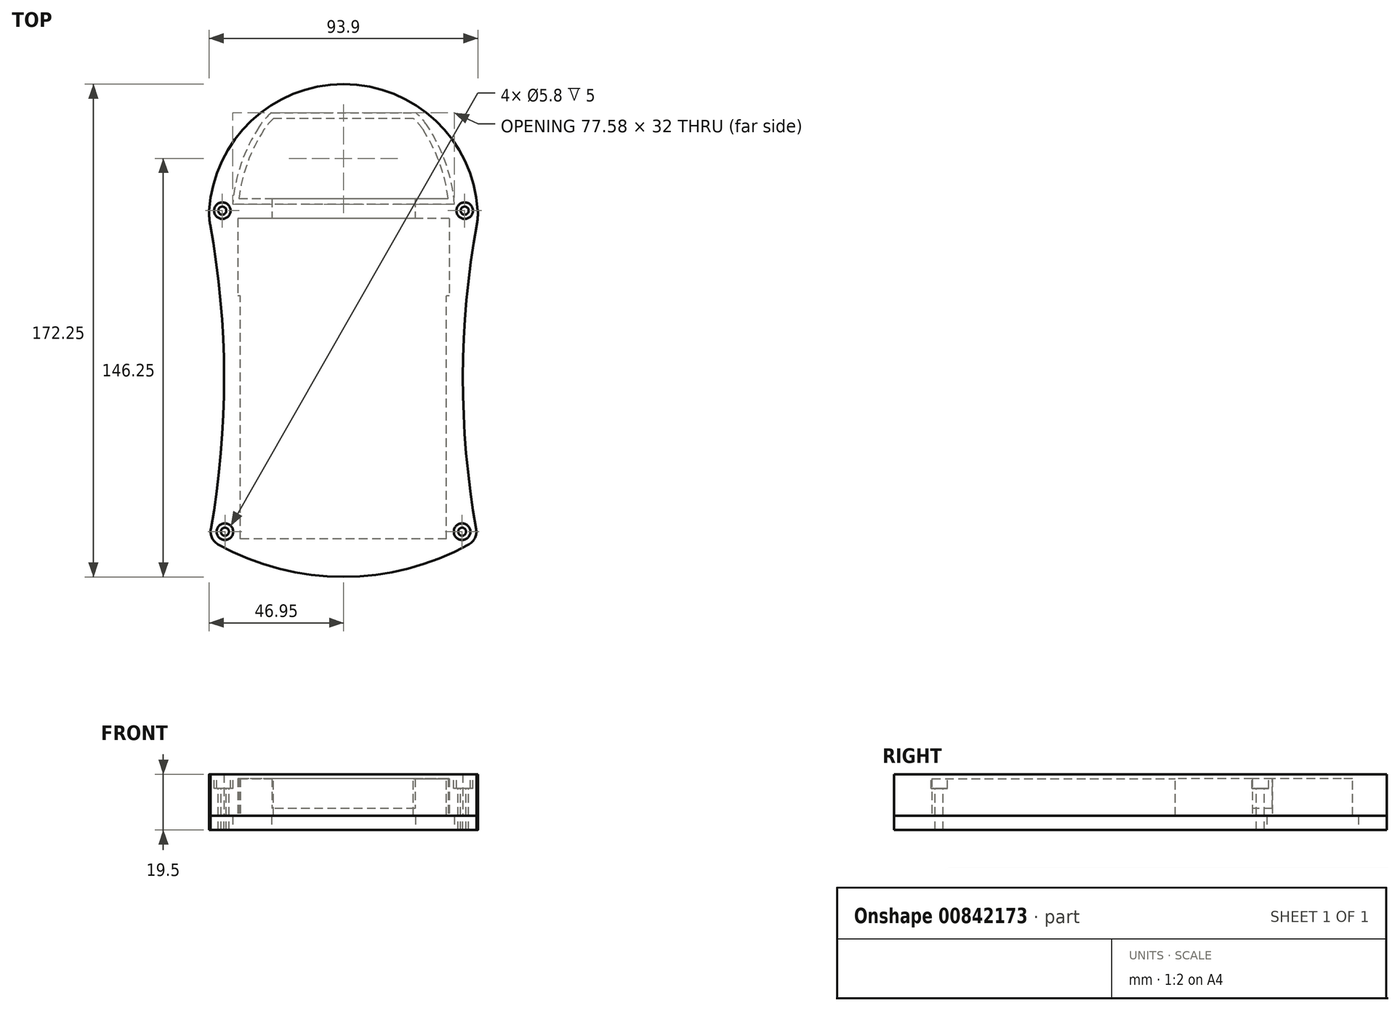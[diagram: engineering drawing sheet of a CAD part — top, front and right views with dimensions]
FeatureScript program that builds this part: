
annotation { "Feature Type Name" : "Feature", "Feature Type Description" : "" }
export const myFeature = defineFeature(function(context is Context, id is Id, definition is map)
    precondition{}
    {
        {
            var Q0;
            Q0=qCreatedBy(makeId("Top.planeOp"),FACE);
            var sketch = newSketch(context, id + "F0", { "sketchPlane" : qUnion([Q0])});
            skLineSegment(sketch, "E0.bottom", {"start": v(36, -56) * mm, "end": v(-36, -56) * mm});
            skLineSegment(sketch, "E0.top", {"start": v(36, 56) * mm, "end": v(-36, 56) * mm});
            skLineSegment(sketch, "E0.left", {"start": v(36, -56) * mm, "end": v(36, 56) * mm});
            skLineSegment(sketch, "E0.right", {"start": v(-36, -56) * mm, "end": v(-36, 56) * mm});
            skPoint(sketch, "E0.middle", {"position": v(0, 0) * mm});
            skArc(sketch, "E1", {"start": v(47, 56) * mm, "mid": v(0, 103) * mm, "end": v(-47, 56) * mm});
            skArc(sketch, "E2", {"start": v(-47, -56) * mm, "mid": v(-41.73, 0) * mm, "end": v(-47, 56) * mm});
            skLineSegment(sketch, "E3", {"start": v(0, 117.63) * mm, "end": v(0, -101.58) * mm, "construction": true});
            skLineSegment(sketch, "E4", {"start": v(-114.42, 0) * mm, "end": v(113.04, 0) * mm, "construction": true});
            skArc(sketch, "E5.MirrorCS", {"start": v(47, -56) * mm, "mid": v(0, -103) * mm, "end": v(-47, -56) * mm});
            skArc(sketch, "E6.MirrorCS", {"start": v(47, -56) * mm, "mid": v(41.73, 0) * mm, "end": v(47, 56) * mm});
            skSolve(sketch);
        }
        {
            var Q0;
            Q0=makeQuery(id+"F0.imprint","IMPRINT",FACE,{"disambiguationData":[TD([[makeQuery(id+"F0.imprint","IMPRINT",EDGE,{"derivedFrom":sQuery(id+"F0.wireOp",EDGE,"E0.bottom")}),1.0]])]});
            extrude(context, id + "F1", {"entities" : qUnion([Q0]), "depth" : 14.5 * mm, "offsetDistance" : 25 * mm});
        }
        {
            var Q0;
            Q0=makeQuery(id+"F1.opExtrude","CAP_FACE",FACE,{"disambiguationData":[OSD([sQuery(id+"F0.wireOp",EDGE,"E0.bottom"),sQuery(id+"F0.wireOp",EDGE,"E0.top"),sQuery(id+"F0.wireOp",EDGE,"E0.left"),sQuery(id+"F0.wireOp",EDGE,"E0.right"),sQuery(id+"F0.wireOp",EDGE,"E1"),sQuery(id+"F0.wireOp",EDGE,"E2"),sQuery(id+"F0.wireOp",EDGE,"E5.MirrorCS"),sQuery(id+"F0.wireOp",EDGE,"E6.MirrorCS")])],"isStart":false});
            var sketch = newSketch(context, id + "F2", { "sketchPlane" : qUnion([Q0])});
            skLineSegment(sketch, "E7.bottom", {"start": v(36, -56) * mm, "end": v(-36, -56) * mm});
            skLineSegment(sketch, "E7.top", {"start": v(36, 56) * mm, "end": v(-36, 56) * mm});
            skLineSegment(sketch, "E7.left", {"start": v(36, -56) * mm, "end": v(36, 56) * mm});
            skLineSegment(sketch, "E7.right", {"start": v(-36, -56) * mm, "end": v(-36, 56) * mm});
            skPoint(sketch, "E7.middle", {"position": v(0, 0) * mm});
            skSolve(sketch);
        }
        {
            var Q0;
            Q0 = qSketchRegion(id + "F2", true);
            extrude(context, id + "F3", {"entities" : qUnion([Q0]), "operationType" : NewBodyOperationType.ADD, "oppositeDirection" : true, "depth" : 1.5 * mm, "offsetDistance" : 25 * mm});
        }
        {
            var Q0;
            Q0=makeQuery(id+"F1.opExtrude","CAP_FACE",FACE,{"disambiguationData":[OSD([sQuery(id+"F0.wireOp",EDGE,"E0.bottom"),sQuery(id+"F0.wireOp",EDGE,"E0.top"),sQuery(id+"F0.wireOp",EDGE,"E0.left"),sQuery(id+"F0.wireOp",EDGE,"E0.right"),sQuery(id+"F0.wireOp",EDGE,"E1"),sQuery(id+"F0.wireOp",EDGE,"E2"),sQuery(id+"F0.wireOp",EDGE,"E5.MirrorCS"),sQuery(id+"F0.wireOp",EDGE,"E6.MirrorCS")])],"isStart":true});
            var sketch = newSketch(context, id + "F4", { "sketchPlane" : qUnion([Q0])});
            skLineSegment(sketch, "E8", {"start": v(0, -56) * mm, "end": v(0, -29) * mm, "construction": true});
            skLineSegment(sketch, "E9.bottom", {"start": v(37, -56) * mm, "end": v(-37, -56) * mm});
            skLineSegment(sketch, "E9.top", {"start": v(37, -29) * mm, "end": v(-37, -29) * mm});
            skLineSegment(sketch, "E9.left", {"start": v(37, -56) * mm, "end": v(37, -29) * mm});
            skLineSegment(sketch, "E9.right", {"start": v(-37, -56) * mm, "end": v(-37, -29) * mm});
            skPoint(sketch, "E9.middle", {"position": v(0, -42.5) * mm});
            skSolve(sketch);
        }
        {
            var Q0;
            Q0 = qSketchRegion(id + "F4", true);
            var Q1;
            Q1=makeQuery(id+"F3.opExtrude","CAP_FACE",FACE,{"disambiguationData":[OSD([sQuery(id+"F2.wireOp",EDGE,"E7.bottom"),sQuery(id+"F2.wireOp",EDGE,"E7.top"),sQuery(id+"F2.wireOp",EDGE,"E7.left"),sQuery(id+"F2.wireOp",EDGE,"E7.right")])],"isStart":false});
            extrude(context, id + "F5", {"entities" : qUnion([Q0]), "operationType" : NewBodyOperationType.REMOVE, "endBound" : BoundingType.UP_TO_SURFACE, "oppositeDirection" : true, "depth" : 25 * mm, "endBoundEntityFace" : qUnion([Q1]), "offsetDistance" : 25 * mm});
        }
        {
            var Q0;
            Q0=makeQuery(id+"F1.opExtrude","CAP_FACE",FACE,{"disambiguationData":[OSD([sQuery(id+"F0.wireOp",EDGE,"E0.bottom"),sQuery(id+"F0.wireOp",EDGE,"E0.top"),sQuery(id+"F0.wireOp",EDGE,"E0.left"),sQuery(id+"F0.wireOp",EDGE,"E0.right"),sQuery(id+"F0.wireOp",EDGE,"E1"),sQuery(id+"F0.wireOp",EDGE,"E2"),sQuery(id+"F0.wireOp",EDGE,"E5.MirrorCS"),sQuery(id+"F0.wireOp",EDGE,"E6.MirrorCS")])],"isStart":true});
            var sketch = newSketch(context, id + "F6", { "sketchPlane" : qUnion([Q0])});
            skArc(sketch, "E10", {"start": v(47, 56) * mm, "mid": v(0, 69.25) * mm, "end": v(-47, 56) * mm});
            skArc(sketch, "E11.0", {"start": v(47, 56) * mm, "mid": v(0, 103) * mm, "end": v(-47, 56) * mm});
            skSolve(sketch);
        }
        {
            var Q0;
            Q0 = qSketchRegion(id + "F6", true);
            extrude(context, id + "F7", {"entities" : qUnion([Q0]), "operationType" : NewBodyOperationType.REMOVE, "oppositeDirection" : true, "depth" : 25 * mm, "offsetDistance" : 25 * mm});
        }
        {
            var Q0;
            Q0=makeQuery(id+"F1.opExtrude","CAP_FACE",FACE,{"disambiguationData":[OSD([sQuery(id+"F0.wireOp",EDGE,"E0.bottom"),sQuery(id+"F0.wireOp",EDGE,"E0.top"),sQuery(id+"F0.wireOp",EDGE,"E0.left"),sQuery(id+"F0.wireOp",EDGE,"E0.right"),sQuery(id+"F0.wireOp",EDGE,"E1"),sQuery(id+"F0.wireOp",EDGE,"E2"),sQuery(id+"F0.wireOp",EDGE,"E5.MirrorCS"),sQuery(id+"F0.wireOp",EDGE,"E6.MirrorCS")])],"isStart":true});
            var sketch = newSketch(context, id + "F8", { "sketchPlane" : qUnion([Q0])});
            skArc(sketch, "E12", {"start": v(27.76, -87.12) * mm, "mid": v(33.54, -75.56) * mm, "end": v(36.57, -63) * mm});
            skLineSegment(sketch, "E13", {"start": v(0, 109.51) * mm, "end": v(0, -146.95) * mm, "construction": true});
            skArc(sketch, "E14.MirrorCS", {"start": v(-27.76, -87.12) * mm, "mid": v(-33.54, -75.56) * mm, "end": v(-36.57, -63) * mm});
            skLineSegment(sketch, "E15", {"start": v(-36.57, -63) * mm, "end": v(36.57, -63) * mm});
            skPoint(sketch, "E16.orphan", {"position": v(-47, -56) * mm});
            skPoint(sketch, "E17.orphan", {"position": v(47, -56) * mm});
            skPoint(sketch, "E18.orphan", {"position": v(37, -56) * mm});
            skPoint(sketch, "E19.orphan", {"position": v(-37, -56) * mm});
            skArc(sketch, "E20.0", {"start": v(20.57, -93.76) * mm, "mid": v(0, -99) * mm, "end": v(-20.57, -93.76) * mm});
            skPoint(sketch, "E21.orphan", {"position": v(-16, -100.2) * mm});
            skPoint(sketch, "E22.orphan", {"position": v(16, -100.2) * mm});
            skPoint(sketch, "E23.visualSharp", {"position": v(-25, -90.99) * mm});
            skArc(sketch, "E23.filletArc", {"start": v(-27.76, -87.12) * mm, "mid": v(-24.57, -90.89) * mm, "end": v(-20.57, -93.76) * mm});
            skPoint(sketch, "E24.visualSharp", {"position": v(25, -90.99) * mm});
            skArc(sketch, "E24.filletArc", {"start": v(20.57, -93.76) * mm, "mid": v(24.57, -90.89) * mm, "end": v(27.76, -87.12) * mm});
            skSolve(sketch);
        }
        {
            var Q0;
            Q0 = qSketchRegion(id + "F8", true);
            extrude(context, id + "F9", {"entities" : qUnion([Q0]), "operationType" : NewBodyOperationType.REMOVE, "oppositeDirection" : true, "depth" : 13 * mm, "offsetDistance" : 25 * mm});
        }
        {
            var Q0;
            Q0=makeQuery(id+"F1.opExtrude","SWEPT_EDGE",EDGE,{"disambiguationData":[OSD([sQuery(id+"F0.wireOp",EDGE,"E1"),sQuery(id+"F0.wireOp",EDGE,"E2")])]});
            var Q1;
            Q1=makeQuery(id+"F1.opExtrude","SWEPT_EDGE",EDGE,{"disambiguationData":[OSD([sQuery(id+"F0.wireOp",EDGE,"E1"),sQuery(id+"F0.wireOp",EDGE,"E6.MirrorCS")])]});
            fillet(context, id + "F10", {"entities" : qUnion([Q0, Q1]), "radius" : 20 * mm, "tangentPropagation" : true, "allowEdgeOverflow" : false});
        }
        {
            var Q0;
            {var subQ0=sQuery(id+"F0.wireOp",EDGE,"E6.MirrorCS");Q0=makeQuery(id+"F7.boolean.opBoolean","MERGE",EDGE,{"derivedFrom":[makeQuery(id+"F1.opExtrude","SWEPT_EDGE",EDGE,{"disambiguationData":[OSD([sQuery(id+"F0.wireOp",EDGE,"E5.MirrorCS"),subQ0])]}),makeQuery(id+"F7.opExtrude","SWEPT_EDGE",EDGE,{"disambiguationData":[OSD([subQ0,sQuery(id+"F6.wireOp",EDGE,"E10"),sQuery(id+"F6.wireOp",EDGE,"E11.0")])]})]});}
            var Q1;
            {var subQ0=sQuery(id+"F0.wireOp",EDGE,"E2");Q1=makeQuery(id+"F7.boolean.opBoolean","MERGE",EDGE,{"derivedFrom":[makeQuery(id+"F1.opExtrude","SWEPT_EDGE",EDGE,{"disambiguationData":[OSD([subQ0,sQuery(id+"F0.wireOp",EDGE,"E5.MirrorCS")])]}),makeQuery(id+"F7.opExtrude","SWEPT_EDGE",EDGE,{"disambiguationData":[OSD([subQ0,sQuery(id+"F6.wireOp",EDGE,"E10"),sQuery(id+"F6.wireOp",EDGE,"E11.0")])]})]});}
            fillet(context, id + "F11", {"entities" : qUnion([Q0, Q1]), "radius" : 5 * mm, "tangentPropagation" : true, "allowEdgeOverflow" : false});
        }
        {
            var Q0;
            Q0=makeQuery(id+"F3.boolean.opBoolean","MERGE",FACE,{"derivedFrom":[makeQuery(id+"F1.opExtrude","CAP_FACE",FACE,{"disambiguationData":[OSD([sQuery(id+"F0.wireOp",EDGE,"E0.bottom"),sQuery(id+"F0.wireOp",EDGE,"E0.top"),sQuery(id+"F0.wireOp",EDGE,"E0.left"),sQuery(id+"F0.wireOp",EDGE,"E0.right"),sQuery(id+"F0.wireOp",EDGE,"E1"),sQuery(id+"F0.wireOp",EDGE,"E2"),sQuery(id+"F0.wireOp",EDGE,"E5.MirrorCS"),sQuery(id+"F0.wireOp",EDGE,"E6.MirrorCS")])],"isStart":false}),makeQuery(id+"F3.opExtrude","CAP_FACE",FACE,{"disambiguationData":[OSD([sQuery(id+"F2.wireOp",EDGE,"E7.bottom"),sQuery(id+"F2.wireOp",EDGE,"E7.top"),sQuery(id+"F2.wireOp",EDGE,"E7.left"),sQuery(id+"F2.wireOp",EDGE,"E7.right")])],"isStart":true})]});
            var sketch = newSketch(context, id + "F12", { "sketchPlane" : qUnion([Q0])});
            skCircle(sketch, "E25", {"center": v(-42.35, 58.78) * mm, "radius": 2.9 * mm});
            skLineSegment(sketch, "E26", {"start": v(0, 101.03) * mm, "end": v(0, -86.28) * mm, "construction": true});
            skCircle(sketch, "E27.MirrorC", {"center": v(42.35, 58.78) * mm, "radius": 2.9 * mm});
            skCircle(sketch, "E28", {"center": v(-41.45, -53.46) * mm, "radius": 2.9 * mm});
            skCircle(sketch, "E29.MirrorC", {"center": v(41.45, -53.46) * mm, "radius": 2.9 * mm});
            skSolve(sketch);
        }
        {
            var Q0;
            Q0 = qSketchRegion(id + "F12", true);
            extrude(context, id + "F13", {"entities" : qUnion([Q0]), "operationType" : NewBodyOperationType.REMOVE, "oppositeDirection" : true, "depth" : 5 * mm, "offsetDistance" : 25 * mm});
        }
        {
            var Q0;
            Q0=makeQuery(id+"F13.boolean.opBoolean","COPY",FACE,{"derivedFrom":makeQuery(id+"F13.opExtrude","CAP_FACE",FACE,{"disambiguationData":[OSD([sQuery(id+"F12.wireOp",EDGE,"E25")])],"isStart":false})});
            var sketch = newSketch(context, id + "F14", { "sketchPlane" : qUnion([Q0])});
            skCircle(sketch, "E30", {"center": v(-42.35, 58.78) * mm, "radius": 1.4 * mm});
            skLineSegment(sketch, "E31", {"start": v(0, 85.8) * mm, "end": v(0, -75.06) * mm, "construction": true});
            skCircle(sketch, "E32", {"center": v(-41.45, -53.46) * mm, "radius": 1.4 * mm});
            skCircle(sketch, "E33.MirrorC", {"center": v(42.35, 58.78) * mm, "radius": 1.4 * mm});
            skCircle(sketch, "E34.MirrorC", {"center": v(41.45, -53.46) * mm, "radius": 1.4 * mm});
            skSolve(sketch);
        }
        {
            var Q0;
            Q0 = qSketchRegion(id + "F14", true);
            extrude(context, id + "F15", {"entities" : qUnion([Q0]), "operationType" : NewBodyOperationType.REMOVE, "oppositeDirection" : true, "depth" : 25 * mm, "offsetDistance" : 25 * mm});
        }
        {
            var Q0;
            Q0=makeQuery(id+"F5.boolean.opBoolean","MERGE",FACE,{"derivedFrom":[makeQuery(id+"F1.opExtrude","SWEPT_FACE",FACE,{"disambiguationData":[OSD([sQuery(id+"F0.wireOp",EDGE,"E0.top")])]}),makeQuery(id+"F5.opExtrude","SWEPT_FACE",FACE,{"disambiguationData":[OSD([sQuery(id+"F4.wireOp",EDGE,"E9.bottom")])]})]});
            var sketch = newSketch(context, id + "F16", { "sketchPlane" : qUnion([Q0])});
            skLineSegment(sketch, "E35.bottom", {"start": v(-25, 13) * mm, "end": v(25, 13) * mm});
            skLineSegment(sketch, "E35.left", {"start": v(-25, 13) * mm, "end": v(-25, 2.5) * mm});
            skLineSegment(sketch, "E35.right", {"start": v(25, 13) * mm, "end": v(25, 2.5) * mm});
            skPoint(sketch, "E35.middle", {"position": v(0, 6.5) * mm});
            skLineSegment(sketch, "E36", {"start": v(25, 2.5) * mm, "end": v(-25, 2.5) * mm});
            skPoint(sketch, "E37.orphan", {"position": v(25, 0) * mm});
            skPoint(sketch, "E38.orphan", {"position": v(-25, 0) * mm});
            skSolve(sketch);
        }
        {
            var Q0;
            Q0 = qSketchRegion(id + "F16", true);
            extrude(context, id + "F17", {"entities" : qUnion([Q0]), "operationType" : NewBodyOperationType.REMOVE, "oppositeDirection" : true, "depth" : 25 * mm, "offsetDistance" : 25 * mm});
        }
        {
            var Q0;
            Q0=makeQuery(id+"F9.boolean.opBoolean","COPY",FACE,{"derivedFrom":makeQuery(id+"F9.opExtrude","CAP_FACE",FACE,{"disambiguationData":[OSD([sQuery(id+"F8.wireOp",EDGE,"E12"),sQuery(id+"F8.wireOp",EDGE,"E14.MirrorCS"),sQuery(id+"F8.wireOp",EDGE,"E15"),sQuery(id+"F8.wireOp",EDGE,"E20.0"),sQuery(id+"F8.wireOp",EDGE,"E23.filletArc"),sQuery(id+"F8.wireOp",EDGE,"E24.filletArc")])],"isStart":false})});
            var sketch = newSketch(context, id + "F18", { "sketchPlane" : qUnion([Q0])});
            skPoint(sketch, "E39", {"position": v(24.45, -91) * mm});
            skLineSegment(sketch, "E40", {"start": v(24.45, -91) * mm, "end": v(-24.45, -91) * mm});
            skArc(sketch, "E41.0", {"start": v(-24.45, -91) * mm, "mid": v(-22.6, -92.5) * mm, "end": v(-20.57, -93.76) * mm});
            skArc(sketch, "E42.0", {"start": v(20.57, -93.76) * mm, "mid": v(0, -99) * mm, "end": v(-20.57, -93.76) * mm});
            skArc(sketch, "E43.0", {"start": v(20.57, -93.76) * mm, "mid": v(22.6, -92.5) * mm, "end": v(24.45, -91) * mm});
            skPoint(sketch, "E44.orphan", {"position": v(-27.76, -87.12) * mm});
            skPoint(sketch, "E45.orphan", {"position": v(27.76, -87.12) * mm});
            skSolve(sketch);
        }
        {
            var Q0;
            Q0 = qSketchRegion(id + "F18", true);
            var Q1;
            Q1=makeQuery(id+"F1.opExtrude","CAP_FACE",FACE,{"disambiguationData":[OSD([sQuery(id+"F0.wireOp",EDGE,"E0.bottom"),sQuery(id+"F0.wireOp",EDGE,"E0.top"),sQuery(id+"F0.wireOp",EDGE,"E0.left"),sQuery(id+"F0.wireOp",EDGE,"E0.right"),sQuery(id+"F0.wireOp",EDGE,"E1"),sQuery(id+"F0.wireOp",EDGE,"E2"),sQuery(id+"F0.wireOp",EDGE,"E5.MirrorCS"),sQuery(id+"F0.wireOp",EDGE,"E6.MirrorCS")])],"isStart":true});
            extrude(context, id + "F19", {"entities" : qUnion([Q0]), "operationType" : NewBodyOperationType.ADD, "endBound" : BoundingType.UP_TO_SURFACE, "depth" : 25 * mm, "endBoundEntityFace" : qUnion([Q1]), "offsetDistance" : 25 * mm});
        }
        {
            var Q0;
            {var subQ0=sQuery(id+"F0.wireOp",EDGE,"E6.MirrorCS");var subQ1=sQuery(id+"F0.wireOp",EDGE,"E5.MirrorCS");var subQ2=sQuery(id+"F0.wireOp",EDGE,"E2");var subQ3=sQuery(id+"F0.wireOp",EDGE,"E1");var subQ4=sQuery(id+"F0.wireOp",EDGE,"E0.right");var subQ5=sQuery(id+"F0.wireOp",EDGE,"E0.left");var subQ6=sQuery(id+"F0.wireOp",EDGE,"E0.top");var subQ7=sQuery(id+"F0.wireOp",EDGE,"E0.bottom");Q0=makeQuery(id+"F19.boolean.opBoolean","MERGE",FACE,{"derivedFrom":[makeQuery(id+"F1.opExtrude","CAP_FACE",FACE,{"disambiguationData":[OSD([subQ7,subQ6,subQ5,subQ4,subQ3,subQ2,subQ1,subQ0])],"isStart":true}),makeQuery(id+"F19.opExtrude","CAP_FACE",FACE,{"disambiguationData":[OSD([subQ7,subQ6,subQ5,subQ4,subQ3,subQ2,subQ1,subQ0])],"isStart":false})]});}
            var sketch = newSketch(context, id + "F20", { "sketchPlane" : qUnion([Q0])});
            skArc(sketch, "E46.0.0", {"start": v(46.63, -54) * mm, "mid": v(41.73, -0.72) * mm, "end": v(46.37, 52.58) * mm});
            skArc(sketch, "E46.0.1", {"start": v(46.37, 52.58) * mm, "mid": v(45.97, 55.6) * mm, "end": v(43.89, 57.82) * mm});
            skArc(sketch, "E46.0.2", {"start": v(43.89, 57.82) * mm, "mid": v(0, 69.25) * mm, "end": v(-43.89, 57.82) * mm});
            skArc(sketch, "E46.0.3", {"start": v(-43.89, 57.82) * mm, "mid": v(-45.97, 55.6) * mm, "end": v(-46.37, 52.58) * mm});
            skArc(sketch, "E46.0.4", {"start": v(-46.37, 52.58) * mm, "mid": v(-41.73, -0.72) * mm, "end": v(-46.63, -54) * mm});
            skArc(sketch, "E46.0.5", {"start": v(-46.63, -54) * mm, "mid": v(-46.92, -56.38) * mm, "end": v(-46.92, -58.78) * mm});
            skArc(sketch, "E46.0.6", {"start": v(-46.92, -58.78) * mm, "mid": v(0, -103) * mm, "end": v(46.92, -58.78) * mm});
            skArc(sketch, "E46.0.7", {"start": v(46.92, -58.78) * mm, "mid": v(46.92, -56.38) * mm, "end": v(46.63, -54) * mm});
            skCircle(sketch, "E47.0", {"center": v(-42.35, -58.78) * mm, "radius": 1.4 * mm});
            skCircle(sketch, "E48.0", {"center": v(42.35, -58.78) * mm, "radius": 1.4 * mm});
            skCircle(sketch, "E49.0", {"center": v(-41.45, 53.46) * mm, "radius": 1.4 * mm});
            skCircle(sketch, "E50.0", {"center": v(41.45, 53.46) * mm, "radius": 1.4 * mm});
            skSolve(sketch);
        }
        {
            var Q0;
            Q0 = qSketchRegion(id + "F20", true);
            extrude(context, id + "F21", {"entities" : qUnion([Q0]), "depth" : 5 * mm, "offsetDistance" : 25 * mm});
        }
        {
            var Q0;
            Q0=makeQuery(id+"F21.opExtrude","CAP_FACE",FACE,{"disambiguationData":[OSD([sQuery(id+"F20.wireOp",EDGE,"E46.0.0"),sQuery(id+"F20.wireOp",EDGE,"E46.0.1"),sQuery(id+"F20.wireOp",EDGE,"E46.0.2"),sQuery(id+"F20.wireOp",EDGE,"E46.0.3"),sQuery(id+"F20.wireOp",EDGE,"E46.0.4"),sQuery(id+"F20.wireOp",EDGE,"E46.0.5"),sQuery(id+"F20.wireOp",EDGE,"E46.0.6"),sQuery(id+"F20.wireOp",EDGE,"E46.0.7"),sQuery(id+"F20.wireOp",EDGE,"E47.0"),sQuery(id+"F20.wireOp",EDGE,"E48.0"),sQuery(id+"F20.wireOp",EDGE,"E49.0"),sQuery(id+"F20.wireOp",EDGE,"E50.0")])],"isStart":false});
            var sketch = newSketch(context, id + "F22", { "sketchPlane" : qUnion([Q0])});
            skLineSegment(sketch, "E51.0.0", {"start": v(-24.45, -91) * mm, "end": v(24.45, -91) * mm});
            skArc(sketch, "E51.0.1", {"start": v(24.45, -91) * mm, "mid": v(26.23, -89.16) * mm, "end": v(27.76, -87.12) * mm});
            skArc(sketch, "E51.0.2", {"start": v(27.76, -87.12) * mm, "mid": v(33.54, -75.56) * mm, "end": v(36.57, -63) * mm});
            skLineSegment(sketch, "E51.0.3", {"start": v(36.57, -63) * mm, "end": v(-36.57, -63) * mm});
            skArc(sketch, "E51.0.4", {"start": v(-36.57, -63) * mm, "mid": v(-33.54, -75.56) * mm, "end": v(-27.76, -87.12) * mm});
            skArc(sketch, "E51.0.5", {"start": v(-27.76, -87.12) * mm, "mid": v(-26.23, -89.16) * mm, "end": v(-24.45, -91) * mm});
            skArc(sketch, "E52.0", {"start": v(29.43, -88.2) * mm, "mid": v(35.8, -75.18) * mm, "end": v(38.79, -61) * mm});
            skArc(sketch, "E52.1", {"start": v(-38.79, -61) * mm, "mid": v(-35.8, -75.18) * mm, "end": v(-29.43, -88.2) * mm});
            skArc(sketch, "E52.2", {"start": v(-29.43, -88.2) * mm, "mid": v(-27.5, -90.76) * mm, "end": v(-25.2, -93) * mm});
            skLineSegment(sketch, "E52.3", {"start": v(38.79, -61) * mm, "end": v(-38.79, -61) * mm});
            skLineSegment(sketch, "E52.4", {"start": v(-25.2, -93) * mm, "end": v(25.2, -93) * mm});
            skArc(sketch, "E52.5", {"start": v(25.2, -93) * mm, "mid": v(27.5, -90.76) * mm, "end": v(29.43, -88.2) * mm});
            skSolve(sketch);
        }
        {
            var Q0;
            Q0=makeQuery(id+"F22.imprint","IMPRINT",FACE,{"disambiguationData":[TD([[makeQuery(id+"F22.imprint","IMPRINT",EDGE,{"derivedFrom":sQuery(id+"F22.wireOp",EDGE,"E51.0.0")}),-1.0]])]});
            var Q1;
            Q1=makeQuery(id+"F22.imprint","IMPRINT",FACE,{"disambiguationData":[TD([[makeQuery(id+"F22.imprint","IMPRINT",EDGE,{"derivedFrom":sQuery(id+"F22.wireOp",EDGE,"E51.0.0")}),1.0]])]});
            extrude(context, id + "F23", {"entities" : qUnion([Q0, Q1]), "operationType" : NewBodyOperationType.REMOVE, "oppositeDirection" : true, "depth" : 5 * mm, "offsetDistance" : 25 * mm});
        }
    });
